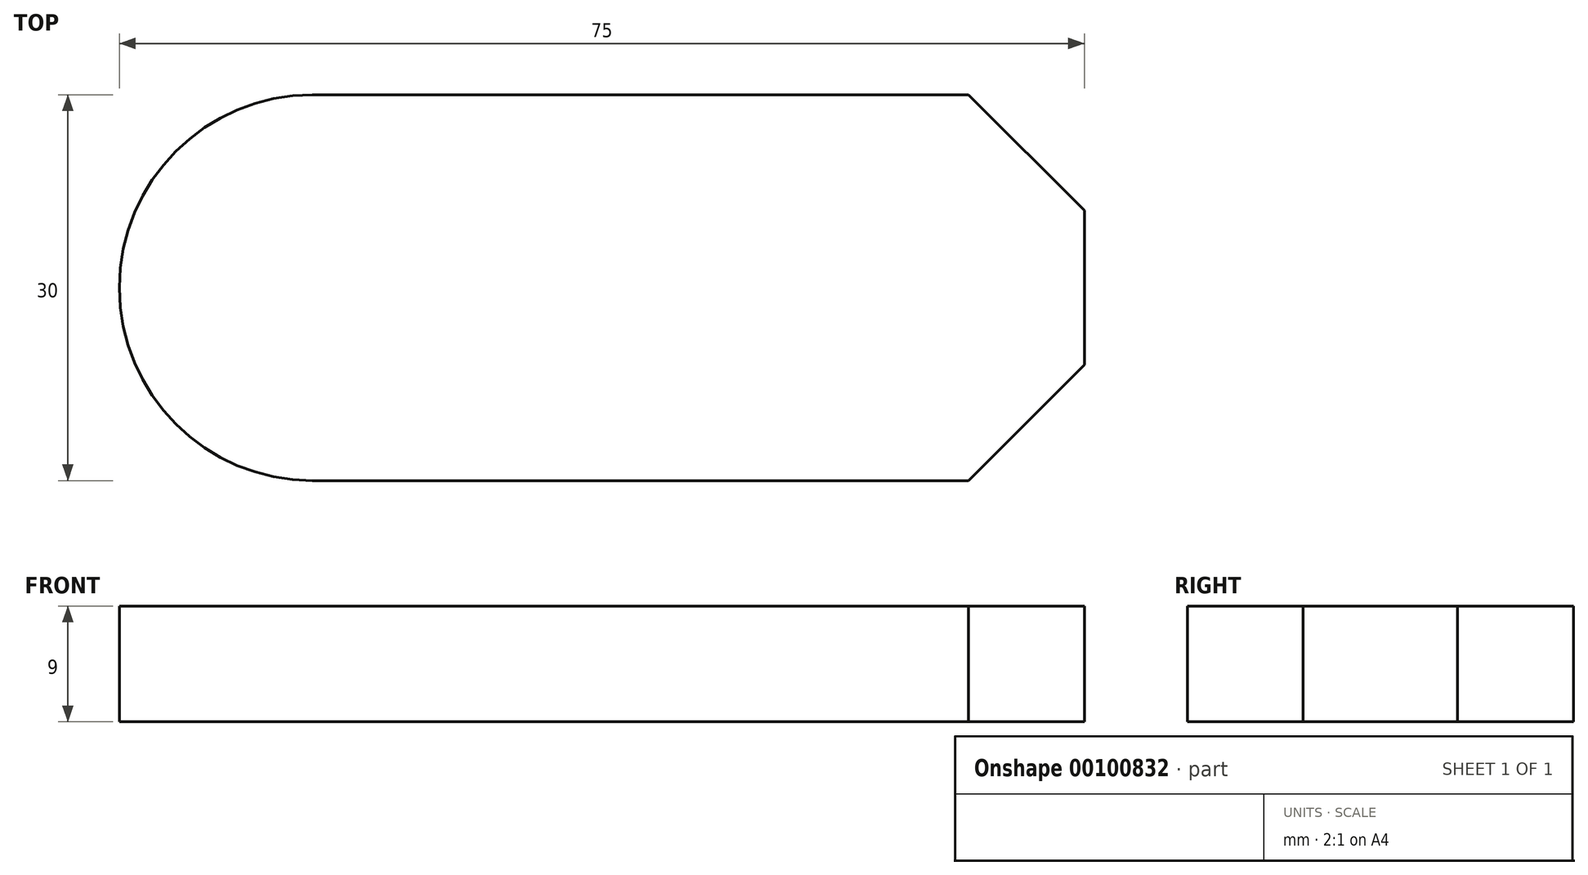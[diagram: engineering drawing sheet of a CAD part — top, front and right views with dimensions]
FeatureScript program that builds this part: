
annotation { "Feature Type Name" : "Feature", "Feature Type Description" : "" }
export const myFeature = defineFeature(function(context is Context, id is Id, definition is map)
    precondition{}
    {
        {
            var Q0;
            Q0=qCreatedBy(makeId("Top.planeOp"),FACE);
            var sketch = newSketch(context, id + "F0", { "sketchPlane" : qUnion([Q0])});
            skLineSegment(sketch, "E0.bottom", {"start": v(0, 0) * mm, "end": v(51, 0) * mm});
            skLineSegment(sketch, "E0.top", {"start": v(0, 30) * mm, "end": v(51, 30) * mm});
            skLineSegment(sketch, "E1", {"start": v(51, 30) * mm, "end": v(60, 21) * mm});
            skLineSegment(sketch, "E2", {"start": v(51, 0) * mm, "end": v(60, 9) * mm});
            skLineSegment(sketch, "E3", {"start": v(60, 21) * mm, "end": v(60, 9) * mm});
            skArc(sketch, "E4", {"start": v(0, 30) * mm, "mid": v(-15, 15) * mm, "end": v(0, 0) * mm});
            skSolve(sketch);
        }
        {
            var Q0;
            Q0=makeQuery(id+"F0.imprint","IMPRINT",FACE,{"disambiguationData":[TD([[makeQuery(id+"F0.imprint","IMPRINT",EDGE,{"derivedFrom":sQuery(id+"F0.wireOp",EDGE,"E0.bottom")}),1.0]])]});
            extrude(context, id + "F1", {"entities" : qUnion([Q0]), "depth" : 9 * mm});
        }
    });
